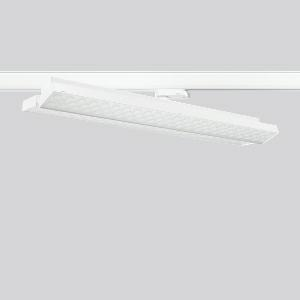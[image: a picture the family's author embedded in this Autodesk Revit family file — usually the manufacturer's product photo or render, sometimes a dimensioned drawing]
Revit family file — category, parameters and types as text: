
# Revit family: tx-move_742163_002_3_c25a
name_source: partatom
category: Lighting Fixtures
units: mm (PartAtom-declared; Revit-internal decimal feet)

## family parameters
Cut with Voids When Loaded = No
Host = Face
Light Source = No
Part Type = Normal
Room Calculation Point = No
Round Connector Dimension = Use Diameter
Shared = No

## types (1)
- MultiLumen 1 (1 x LED Modul 835, 2875 lm, 3500)
    Apparent Load = 41 VA
    CIE Flux Codes = 65 90 98 100 100
    Color Rendering = 80
    Color Temperature = 3500
    Default Elevation = 1800 mm
    Description = Series: TX-MOVE
Multifunctional surface-mounted spotlight for area lighting. Very flat design. Housing: sheet steel, powder-coated. Rotation range: 356°. Swivel range: 90°. Consistent alignment possible with visible tilt scale. High-efficiency LED units with optimum light control thanks to clear plastic (PC) lens optics. Spezielle Mikrostrukturen reduzieren Gelbsaum. Asymmetrical light distribution. With multi adaptor for 3-circuit tracks 230 V. Suitable for Track on ceiling. MultiLumen: Luminous flux adjustable in 3 steps. Factory setting is the highest luminous flux. Environmentally friendly and resource-saving due to replaceable and recyclable components. 
Colour: traffic white, matt (RAL 9016)
Length: 570 mm
Width: 119 mm
Height: 92 mm
Lamp: LED
Socket: without socket
Colour temperature: 3500K
Colour rendering index (CRI): 80
System power: 41 W
Rated luminous flux: 5750 lm
Luminous efficiency: 140 lm/W
System power 2: 57 W
Rated luminous flux 2: 7750 lm
Luminous efficiency 2: 136 lm/W
System power 3: 73 W
Rated luminous flux 3: 9450 lm
Luminous efficiency 3: 129 lm/W
Control gear: Regulated power supply
Protection class: I
Type of protection: IP 20
    Height = 75 mm
    Lamp = 1 x LED Modul 835
    Lamp Light Flux = 2875 lm
    Lamp count = 1
    Length = 569 mm
    Lifetime = 50000 h
    Luminous efficacy = 140 lm/W
    Manufacturer = RZB
    ModVariant = No
    Model = 742163.002.3
    Mounting Place = Ceiling
    Mounting Type = Rail mounted
    Number of Poles = 1
    OnlyDefault = Yes
    Power Factor = 1
    Product Name = TX-MOVE
    Product group = Track mounted projectors
    ProductGroupID = 301
    Protection Class = Protection class I
    Protection Degree = IP 20
    RLX_Detail_Level = 1
    RLX_Emergency_Light_Flux = 0 lm
    RLX_Emergency_Type = 0
    RLX_Emergency_Type_DB = No
    RlxData = <blob elided: 51861 chars, md5=f63df4a2>
    Socket = socket
    Standby Power = 0 W
    System Light Flux = 5750 lm
    System Power = 41 W
    Type Comments = MultiLumen 1
    Type Image = 742162.002.jpg
    URL = http://relux.com
    VarID = multilumen_1
    Voltage = 230 V
    Voltage Range = 220-240 V
    Weight = 0.00 kg
    Width = 119 mm

## geometry (parser evidence)
native form markers: Blend x4, Sweep x16
no freeform markers — native parametric forms only
